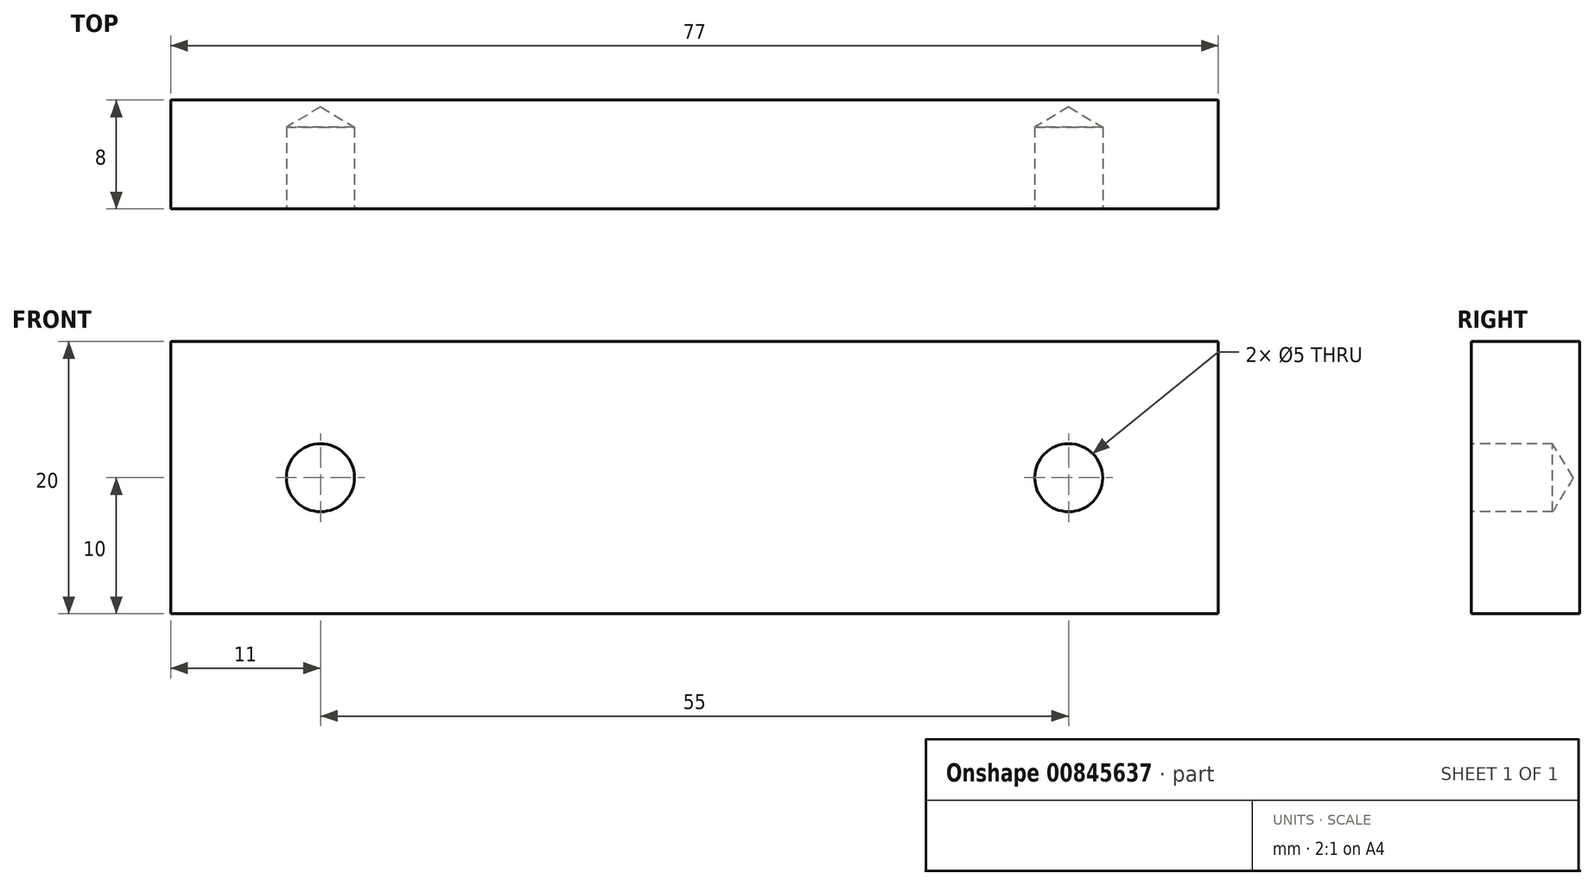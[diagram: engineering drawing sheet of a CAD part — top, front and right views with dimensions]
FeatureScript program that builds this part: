
annotation { "Feature Type Name" : "Feature", "Feature Type Description" : "" }
export const myFeature = defineFeature(function(context is Context, id is Id, definition is map)
    precondition{}
    {
        {
            var Q0;
            Q0=qCreatedBy(makeId("Front.planeOp"),FACE);
            var sketch = newSketch(context, id + "F0", { "sketchPlane" : qUnion([Q0])});
            skLineSegment(sketch, "E0.bottom", {"start": v(38.5, -10) * mm, "end": v(-38.5, -10) * mm});
            skLineSegment(sketch, "E0.top", {"start": v(38.5, 10) * mm, "end": v(-38.5, 10) * mm});
            skLineSegment(sketch, "E0.left", {"start": v(38.5, -10) * mm, "end": v(38.5, 10) * mm});
            skLineSegment(sketch, "E0.right", {"start": v(-38.5, -10) * mm, "end": v(-38.5, 10) * mm});
            skPoint(sketch, "E0.middle", {"position": v(0, 0) * mm});
            skLineSegment(sketch, "E1", {"start": v(-27.5, 0) * mm, "end": v(27.5, 0) * mm, "construction": true});
            skSolve(sketch);
        }
        {
            var Q0;
            Q0=makeQuery(id+"F0.imprint","IMPRINT",FACE,{"disambiguationData":[TD([[makeQuery(id+"F0.imprint","IMPRINT",EDGE,{"derivedFrom":sQuery(id+"F0.wireOp",EDGE,"E0.bottom")}),-1.0]])]});
            extrude(context, id + "F1", {"entities" : qUnion([Q0]), "oppositeDirection" : true, "depth" : 8 * mm, "offsetDistance" : 25 * mm});
        }
        {
            var Q0;
            Q0=sQuery(id+"F0.wireOp",VERTEX,"E1.start");
            var Q1;
            Q1=sQuery(id+"F0.wireOp",VERTEX,"E1.end");
            var Q2;
            Q2=makeQuery(id+"F1.opExtrude","SWEPT_BODY",BODY,{"disambiguationData":[OSD([sQuery(id+"F0.wireOp",EDGE,"E0.bottom"),sQuery(id+"F0.wireOp",EDGE,"E0.top"),sQuery(id+"F0.wireOp",EDGE,"E0.left"),sQuery(id+"F0.wireOp",EDGE,"E0.right")])]});
            hole(context, id + "F2", {"style" : HoleStyle.SIMPLE, "endStyle" : HoleEndStyle.BLIND, "standardTappedOrClearance" : lookupTablePath({ "standard" : "ISO", "engagement" : "75%", "pitch" : "1 mm", "size" : "M6", "type" : "Tapped" }), "standardBlindInLast" : lookupTablePath({ "standard" : "ISO", "engagement" : "75%", "pitch" : "1 mm", "size" : "M6", "type" : "Tapped" }), "holeDiameter" : 5 * mm, "majorDiameter" : 6 * mm, "showTappedDepth" : true, "holeDepth" : 6 * mm, "isTappedThrough" : true, "tappedDepth" : 6 * mm, "tapClearance" : 0, "startFromSketch" : true, "locations" : qUnion([Q0, Q1]), "scope" : qUnion([Q2])});
        }
    });
